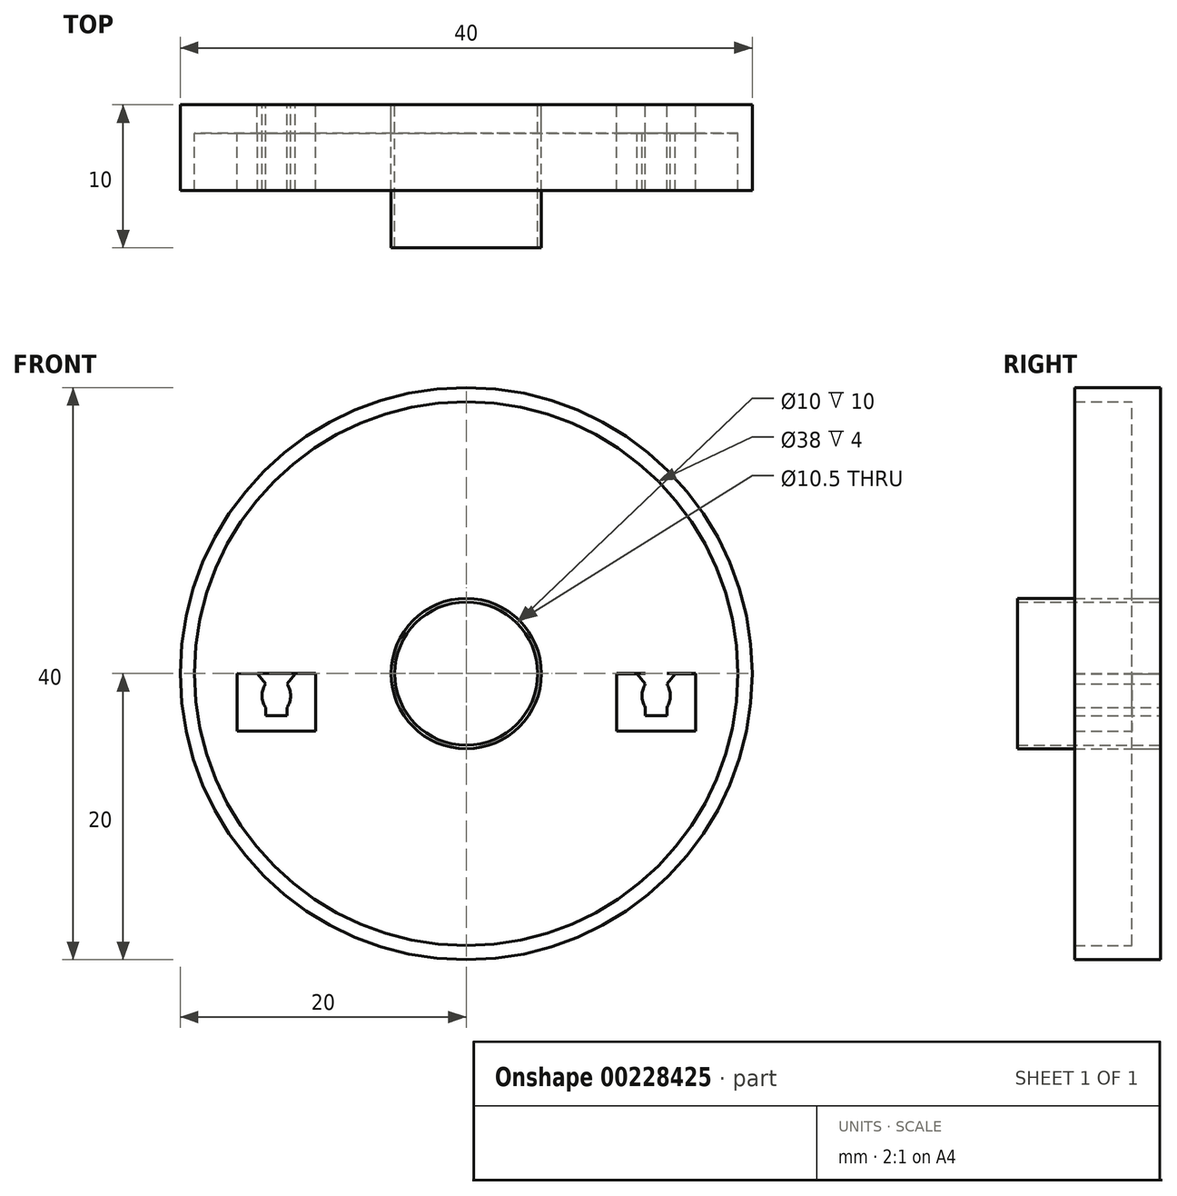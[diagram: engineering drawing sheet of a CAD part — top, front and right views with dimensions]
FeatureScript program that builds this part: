
annotation { "Feature Type Name" : "Feature", "Feature Type Description" : "" }
export const myFeature = defineFeature(function(context is Context, id is Id, definition is map)
    precondition{}
    {
        {
            var Q0;
            Q0=qCreatedBy(makeId("Front.planeOp"),FACE);
            var sketch = newSketch(context, id + "F0", { "sketchPlane" : qUnion([Q0])});
            skCircle(sketch, "E0", {"center": v(0, 0) * mm, "radius": 20 * mm});
            skCircle(sketch, "E1", {"center": v(0, 0) * mm, "radius": 19 * mm});
            skLineSegment(sketch, "E2", {"start": v(-19, 0) * mm, "end": v(19, 0) * mm});
            skLineSegment(sketch, "E3.bottom", {"start": v(-16.03, 0) * mm, "end": v(-14.03, 0) * mm});
            skLineSegment(sketch, "E3.top", {"start": v(-16.03, -4.03) * mm, "end": v(-14.03, -4.03) * mm});
            skLineSegment(sketch, "E3.left", {"start": v(-16.03, 0) * mm, "end": v(-16.03, -4.03) * mm});
            skLineSegment(sketch, "E4.bottom", {"start": v(-14.03, -4.03) * mm, "end": v(-12.53, -4.03) * mm});
            skLineSegment(sketch, "E4.top", {"start": v(-14.03, -2.95) * mm, "end": v(-12.53, -2.95) * mm});
            skLineSegment(sketch, "E4.left", {"start": v(-14.03, -4.03) * mm, "end": v(-14.03, -2.95) * mm});
            skLineSegment(sketch, "E4.right", {"start": v(-12.53, -4.03) * mm, "end": v(-12.53, -2.95) * mm});
            skLineSegment(sketch, "E5.bottom", {"start": v(-12.53, -4.03) * mm, "end": v(-10.53, -4.03) * mm});
            skLineSegment(sketch, "E5.top", {"start": v(-12.53, 0) * mm, "end": v(-10.53, 0) * mm});
            skLineSegment(sketch, "E5.left", {"start": v(-12.53, -4.03) * mm, "end": v(-12.53, -2.37) * mm});
            skLineSegment(sketch, "E5.right", {"start": v(-10.53, -4.03) * mm, "end": v(-10.53, 0) * mm});
            skCircle(sketch, "E6", {"center": v(0, 0) * mm, "radius": 5 * mm});
            skPoint(sketch, "E7.start.orphan", {"position": v(0, 19) * mm});
            skCircle(sketch, "E8", {"center": v(0, 0) * mm, "radius": 4 * mm});
            skCircle(sketch, "E9", {"center": v(0, 0) * mm, "radius": 5.25 * mm});
            skCircle(sketch, "E10", {"center": v(0, 0) * mm, "radius": 7.5 * mm});
            skPoint(sketch, "E11", {"position": v(10.53, -2.03) * mm});
            skPoint(sketch, "E12", {"position": v(12.53, -2.01) * mm});
            skPoint(sketch, "E13", {"position": v(14.03, -2.01) * mm});
            skPoint(sketch, "E14", {"position": v(16.03, -2.03) * mm});
            skPoint(sketch, "E15.orphan", {"position": v(14.03, -4.03) * mm});
            skPoint(sketch, "E16.orphan", {"position": v(12.53, -4.03) * mm});
            skLineSegment(sketch, "E17", {"start": v(14.03, 0) * mm, "end": v(16.03, -0.03) * mm});
            skLineSegment(sketch, "E18", {"start": v(10.53, -0.03) * mm, "end": v(12.53, 0) * mm});
            skLineSegment(sketch, "E19", {"start": v(0, 1.9) * mm, "end": v(0, 0) * mm});
            skLineSegment(sketch, "E20.MirrorCS", {"start": v(-14.03, -0.73) * mm, "end": v(-14.6, 0) * mm});
            skLineSegment(sketch, "E21.MirrorCS", {"start": v(-12.53, -0.73) * mm, "end": v(-11.96, 0) * mm});
            skArc(sketch, "E22", {"start": v(-12.53, -2.37) * mm, "mid": v(-12.29, -1.55) * mm, "end": v(-12.53, -0.73) * mm});
            skArc(sketch, "E23.MirrorCS", {"start": v(-14.03, -2.37) * mm, "mid": v(-14.28, -1.55) * mm, "end": v(-14.03, -0.73) * mm});
            skPoint(sketch, "E24.start.orphan", {"position": v(-13.28, -2.95) * mm});
            skLineSegment(sketch, "E25.trimOffspring", {"start": v(-14.03, -2.37) * mm, "end": v(-14.03, -4.03) * mm});
            skLineSegment(sketch, "E26", {"start": v(-11.96, 0) * mm, "end": v(-10.53, 0) * mm});
            skLineSegment(sketch, "E27", {"start": v(-16.03, 0) * mm, "end": v(-14.6, 0) * mm});
            skPoint(sketch, "E28.MirrorCS.end.orphan", {"position": v(13.28, -2.95) * mm});
            skPoint(sketch, "E29.MirrorCS.end.orphan", {"position": v(14.6, 0) * mm});
            skPoint(sketch, "E29.MirrorCS.start.orphan", {"position": v(14.03, -0.73) * mm});
            skPoint(sketch, "E30.end.orphan", {"position": v(11.96, 0) * mm});
            skPoint(sketch, "E31.trimOffspring.start.orphan", {"position": v(12.53, -0.73) * mm});
            skPoint(sketch, "E32.orphan", {"position": v(16.03, -4.03) * mm});
            skPoint(sketch, "E33.orphan", {"position": v(10.53, -4.03) * mm});
            skPoint(sketch, "E34.orphan", {"position": v(14.03, -2.95) * mm});
            skPoint(sketch, "E35.MirrorCS.end.orphan", {"position": v(12.53, -2.95) * mm});
            skLineSegment(sketch, "E36.MirrorCS", {"start": v(10.53, -4.03) * mm, "end": v(10.53, 0) * mm});
            skLineSegment(sketch, "E37.MirrorCS", {"start": v(12.53, -4.03) * mm, "end": v(10.53, -4.03) * mm});
            skLineSegment(sketch, "E38.MirrorCS", {"start": v(12.53, -4.03) * mm, "end": v(12.53, -2.95) * mm});
            skLineSegment(sketch, "E39.MirrorCS", {"start": v(14.03, -4.03) * mm, "end": v(12.53, -4.03) * mm});
            skLineSegment(sketch, "E40.MirrorCS", {"start": v(16.03, -4.03) * mm, "end": v(14.03, -4.03) * mm});
            skLineSegment(sketch, "E41.MirrorCS", {"start": v(16.03, 0) * mm, "end": v(16.03, -4.03) * mm});
            skLineSegment(sketch, "E42.MirrorCS", {"start": v(14.03, -0.73) * mm, "end": v(14.6, 0) * mm});
            skArc(sketch, "E43.MirrorCS", {"start": v(14.03, -2.37) * mm, "mid": v(14.28, -1.55) * mm, "end": v(14.03, -0.73) * mm});
            skLineSegment(sketch, "E44.MirrorCS", {"start": v(14.03, -2.37) * mm, "end": v(14.03, -4.03) * mm});
            skLineSegment(sketch, "E45.MirrorCS", {"start": v(14.03, -2.95) * mm, "end": v(12.53, -2.95) * mm});
            skLineSegment(sketch, "E46.MirrorCS", {"start": v(12.53, -4.03) * mm, "end": v(12.53, -2.37) * mm});
            skArc(sketch, "E47.MirrorCS", {"start": v(12.53, -2.37) * mm, "mid": v(12.29, -1.55) * mm, "end": v(12.53, -0.73) * mm});
            skLineSegment(sketch, "E48.MirrorCS", {"start": v(12.53, -0.73) * mm, "end": v(11.96, 0) * mm});
            skSolve(sketch);
        }
        {
            var Q0;
            Q0 = qSketchRegion(id + "F0", true);
            var Q1;
            {var subQ3=sQuery(id+"F0.wireOp",EDGE,"E5.bottom");Q1=makeQuery(id+"F0.imprint","IMPRINT",FACE,{"disambiguationData":[TD([[makeQuery(id+"F0.imprint","IMPRINT",EDGE,{"derivedFrom":subQ3}),1.0]])]});}
            var Q2;
            {var subQ0=sQuery(id+"F0.wireOp",EDGE,"E4.bottom");Q2=makeQuery(id+"F0.imprint","IMPRINT",FACE,{"disambiguationData":[TD([[makeQuery(id+"F0.imprint","IMPRINT",EDGE,{"derivedFrom":subQ0}),1.0]])]});}
            var Q3;
            Q3=makeQuery(id+"F0.imprint","IMPRINT",FACE,{"disambiguationData":[TD([[makeQuery(id+"F0.imprint","IMPRINT",EDGE,{"derivedFrom":sQuery(id+"F0.wireOp",EDGE,"a4adbf44-44b8-4eb8-a71d-371475f4c7be0.MirrorCS")}),-1.0]])]});
            var Q4;
            {var subQ1=sQuery(id+"F0.wireOp",EDGE,"E3.top");Q4=makeQuery(id+"F0.imprint","IMPRINT",FACE,{"disambiguationData":[TD([[makeQuery(id+"F0.imprint","IMPRINT",EDGE,{"derivedFrom":subQ1}),1.0]])]});}
            var Q5;
            {var subQ7=sQuery(id+"F0.wireOp",EDGE,"E40.MirrorCS");Q5=makeQuery(id+"F0.imprint","IMPRINT",FACE,{"disambiguationData":[TD([[makeQuery(id+"F0.imprint","IMPRINT",EDGE,{"derivedFrom":subQ7}),-1.0]])]});}
            var Q6;
            {var subQ1=sQuery(id+"F0.wireOp",EDGE,"E37.MirrorCS");Q6=makeQuery(id+"F0.imprint","IMPRINT",FACE,{"disambiguationData":[TD([[makeQuery(id+"F0.imprint","IMPRINT",EDGE,{"derivedFrom":subQ1}),-1.0]])]});}
            var Q7;
            {var subQ0=sQuery(id+"F0.wireOp",EDGE,"E39.MirrorCS");Q7=makeQuery(id+"F0.imprint","IMPRINT",FACE,{"disambiguationData":[TD([[makeQuery(id+"F0.imprint","IMPRINT",EDGE,{"derivedFrom":subQ0}),-1.0]])]});}
            extrude(context, id + "F1", {"entities" : qUnion([Q0, Q1, Q2, Q3, Q4, Q5, Q6, Q7]), "depth" : 6 * mm});
        }
        {
            var Q0;
            Q0 = qSketchRegion(id + "F0", true);
            var Q1;
            Q1=makeQuery(id+"F0.imprint","IMPRINT",FACE,{"disambiguationData":[TD([[makeQuery(id+"F0.imprint","IMPRINT",EDGE,{"derivedFrom":sQuery(id+"F0.wireOp",EDGE,"E1")}),1.0]])]});
            var Q2;
            Q2=makeQuery(id+"F0.imprint","IMPRINT",FACE,{"disambiguationData":[TD([[makeQuery(id+"F0.imprint","IMPRINT",EDGE,{"derivedFrom":sQuery(id+"F0.wireOp",EDGE,"E3.top")}),-1.0]])]});
            var Q3;
            {var subQ3=sQuery(id+"F0.wireOp",EDGE,"E5.bottom");Q3=makeQuery(id+"F0.imprint","IMPRINT",FACE,{"disambiguationData":[TD([[makeQuery(id+"F0.imprint","IMPRINT",EDGE,{"derivedFrom":subQ3}),1.0]])]});}
            var Q4;
            {var subQ0=sQuery(id+"F0.wireOp",EDGE,"E10");var subQ1=sQuery(id+"F0.wireOp",EDGE,"E2");var subQ2=makeQuery(id+"F0.imprint","INTERSECT",VERTEX,{"disambiguationData":[OD(0.0)],"derivedFrom":[subQ1,subQ0]});Q4=makeQuery(id+"F0.imprint","IMPRINT",FACE,{"disambiguationData":[TD([[makeQuery(id+"F0.imprint","IMPRINT",EDGE,{"disambiguationData":[TD([[subQ2,-1.0]])],"derivedFrom":subQ1}),-1.0]])]});}
            var Q5;
            {var subQ0=sQuery(id+"F0.wireOp",EDGE,"E10");var subQ1=sQuery(id+"F0.wireOp",EDGE,"E2");var subQ2=makeQuery(id+"F0.imprint","INTERSECT",VERTEX,{"disambiguationData":[OD(0.0)],"derivedFrom":[subQ1,subQ0]});Q5=makeQuery(id+"F0.imprint","IMPRINT",FACE,{"disambiguationData":[TD([[makeQuery(id+"F0.imprint","IMPRINT",EDGE,{"disambiguationData":[TD([[subQ2,-1.0]])],"derivedFrom":subQ1}),1.0]])]});}
            var Q6;
            {var subQ6=sQuery(id+"F0.wireOp",EDGE,"E3.bottom");Q6=makeQuery(id+"F0.imprint","IMPRINT",FACE,{"disambiguationData":[TD([[makeQuery(id+"F0.imprint","IMPRINT",EDGE,{"derivedFrom":subQ6}),-1.0]])]});}
            var Q7;
            {var subQ2=sQuery(id+"F0.wireOp",EDGE,"E45.MirrorCS");Q7=makeQuery(id+"F0.imprint","IMPRINT",FACE,{"disambiguationData":[TD([[makeQuery(id+"F0.imprint","IMPRINT",EDGE,{"derivedFrom":subQ2}),-1.0]])]});}
            extrude(context, id + "F2", {"entities" : qUnion([Q0, Q1, Q2, Q3, Q4, Q5, Q6, Q7]), "operationType" : NewBodyOperationType.ADD, "depth" : 2 * mm});
        }
        {
            var Q0;
            {var subQ0=sQuery(id+"F0.wireOp",EDGE,"E6");var subQ1=sQuery(id+"F0.wireOp",EDGE,"E2");var subQ2=makeQuery(id+"F0.imprint","INTERSECT",VERTEX,{"disambiguationData":[OD(0.0)],"derivedFrom":[subQ1,subQ0]});Q0=makeQuery(id+"F0.imprint","IMPRINT",FACE,{"disambiguationData":[TD([[makeQuery(id+"F0.imprint","IMPRINT",EDGE,{"disambiguationData":[TD([[subQ2,-1.0]])],"derivedFrom":subQ1}),1.0]])]});}
            var Q1;
            {var subQ0=sQuery(id+"F0.wireOp",EDGE,"E6");var subQ1=sQuery(id+"F0.wireOp",EDGE,"E2");var subQ2=makeQuery(id+"F0.imprint","INTERSECT",VERTEX,{"disambiguationData":[OD(0.0)],"derivedFrom":[subQ1,subQ0]});Q1=makeQuery(id+"F0.imprint","IMPRINT",FACE,{"disambiguationData":[TD([[makeQuery(id+"F0.imprint","IMPRINT",EDGE,{"disambiguationData":[TD([[subQ2,-1.0]])],"derivedFrom":subQ1}),-1.0]])]});}
            extrude(context, id + "F3", {"entities" : qUnion([Q0, Q1]), "depth" : 10 * mm});
        }
    });
